# Revit family: 304_DPCV_1__
name_source: partatom
category: Pipe Accessories
units: mm (PartAtom-declared; Revit-internal decimal feet)

## family parameters
Always vertical = Yes
Cut with Voids When Loaded = No
Part Type = Valve - Breaks Into
Round Connector Dimension = Use Diameter
Shared = No
Work Plane-Based = No

## types (6) — shared parameters
A = 45.00°
CAT0 = Yes
Description = DPCV - Differential Pressure Control Valve
E = 18 mm
L2D_Min = 3048 mm
Manufacturer = FlowCon
QmdConnectorList = 301;D;302;D
R7 = 10 mm  [stored 0.0328084 ft]
S = 10 mm  [stored 0.0328084 ft]
URL = http://flowcon.com
magiPartTypeId = 304
magiProductFamilyId = DPCV.1.*
zero-valued in all types: MC_Default_elevation

## per-type parameters (varying)
- DPCV.1.1.C.I: CenSd_SW2_6=28 mm  [stored 0.0918635 ft]; CenSd_SW_6=24 mm; D=15 mm; H3=16 mm; H3__ve=-16 mm; H4=48 mm; H41=38 mm; H5=32 mm; H6=17 mm; H7=34 mm; H8=56 mm; L1=15 mm  [stored 0.0492126 ft]; L1__ve=-15 mm  [stored -0.0492126 ft]; L2=23 mm; L2D=75 mm; L3=45 mm  [stored 0.147638 ft]; LL=38 mm; R1=17 mm; R2=28 mm  [stored 0.0918635 ft]; R3=22 mm; R4=30 mm  [stored 0.0984252 ft]; R5=15 mm  [stored 0.0492126 ft]; R6=22 mm; SW=28 mm  [stored 0.0918635 ft]; SW2=32 mm; W=44 mm; W2D=15 mm  [stored 0.0492126 ft]; magiProductId=DPCV.1.1
- DPCV.1.6.C.I: CenSd_SW2_6=45 mm  [stored 0.147638 ft]; CenSd_SW_6=39 mm; D=50 mm; H3=23 mm; H3__ve=-23 mm; H4=68 mm; H41=58 mm; H5=46 mm; H6=27 mm; H7=54 mm; H8=97 mm; L1=30 mm  [stored 0.0984252 ft]; L1__ve=-30 mm; L2=45 mm  [stored 0.147638 ft]; L2D=150 mm; L3=90 mm; LL=75 mm; R1=28 mm  [stored 0.0918635 ft]; R2=45 mm  [stored 0.147638 ft]; R3=29 mm; R4=41 mm; R5=20 mm; R6=29 mm; SW=45 mm  [stored 0.147638 ft]; SW2=52 mm; W=59 mm; W2D=50 mm; magiProductId=DPCV.1.6
- DPCV.1.5.C.I: CenSd_SW2_6=36 mm; CenSd_SW_6=31 mm; D=40 mm; H3=22 mm; H3__ve=-22 mm; H4=67 mm; H41=57 mm; H5=45 mm  [stored 0.147638 ft]; H6=22 mm; H7=43 mm; H8=79 mm; L1=24 mm; L1__ve=-24 mm; L2=36 mm; L2D=120 mm; L3=72 mm; LL=60 mm; R1=22 mm; R2=36 mm; R3=29 mm; R4=41 mm; R5=20 mm; R6=29 mm; SW=36 mm; SW2=41 mm; W=59 mm; W2D=40 mm; magiProductId=DPCV.1.5
- DPCV.1.4.C.I: CenSd_SW2_6=35 mm; CenSd_SW_6=30 mm  [stored 0.0984252 ft]; D=32 mm; H3=22 mm; H3__ve=-22 mm; H4=65 mm; H41=55 mm; H5=43 mm; H6=21 mm; H7=42 mm; H8=77 mm; L1=22 mm; L1__ve=-22 mm; L2=33 mm; L2D=110 mm; L3=66 mm; LL=55 mm; R1=22 mm; R2=35 mm; R3=29 mm; R4=41 mm; R5=20 mm; R6=29 mm; SW=35 mm; SW2=40 mm; W=59 mm; W2D=32 mm; magiProductId=DPCV.1.4
- DPCV.1.3.C.I: CenSd_SW2_6=28 mm  [stored 0.0918635 ft]; CenSd_SW_6=24 mm; D=25 mm; H3=16 mm; H3__ve=-16 mm; H4=49 mm; H41=39 mm; H5=33 mm; H6=17 mm; H7=34 mm; H8=58 mm; L1=18 mm; L1__ve=-18 mm; L2=27 mm; L2D=90 mm; L3=54 mm; LL=45 mm  [stored 0.147638 ft]; R1=17 mm; R2=28 mm  [stored 0.0918635 ft]; R3=22 mm; R4=30 mm  [stored 0.0984252 ft]; R5=15 mm  [stored 0.0492126 ft]; R6=22 mm; SW=28 mm  [stored 0.0918635 ft]; SW2=32 mm; W=44 mm; W2D=25 mm  [stored 0.082021 ft]; magiProductId=DPCV.1.3
- DPCV.1.2.C.I: CenSd_SW2_6=28 mm  [stored 0.0918635 ft]; CenSd_SW_6=24 mm; D=20 mm; H3=16 mm; H3__ve=-16 mm; H4=48 mm; H41=38 mm; H5=32 mm; H6=17 mm; H7=34 mm; H8=56 mm; L1=16 mm; L1__ve=-16 mm; L2=24 mm; L2D=80 mm; L3=48 mm; LL=40 mm; R1=17 mm; R2=28 mm  [stored 0.0918635 ft]; R3=22 mm; R4=30 mm  [stored 0.0984252 ft]; R5=15 mm  [stored 0.0492126 ft]; R6=22 mm; SW=28 mm  [stored 0.0918635 ft]; SW2=32 mm; W=44 mm; W2D=20 mm; magiProductId=DPCV.1.2

note: column(s) folded — value = type name in every type: magiProductCode

note: [stored X ft] marks values corroborated as IEEE doubles in the binary element streams (Revit-internal decimal feet)

## geometry (parser evidence)
native form markers: Sweep x2
no freeform markers — native parametric forms only
